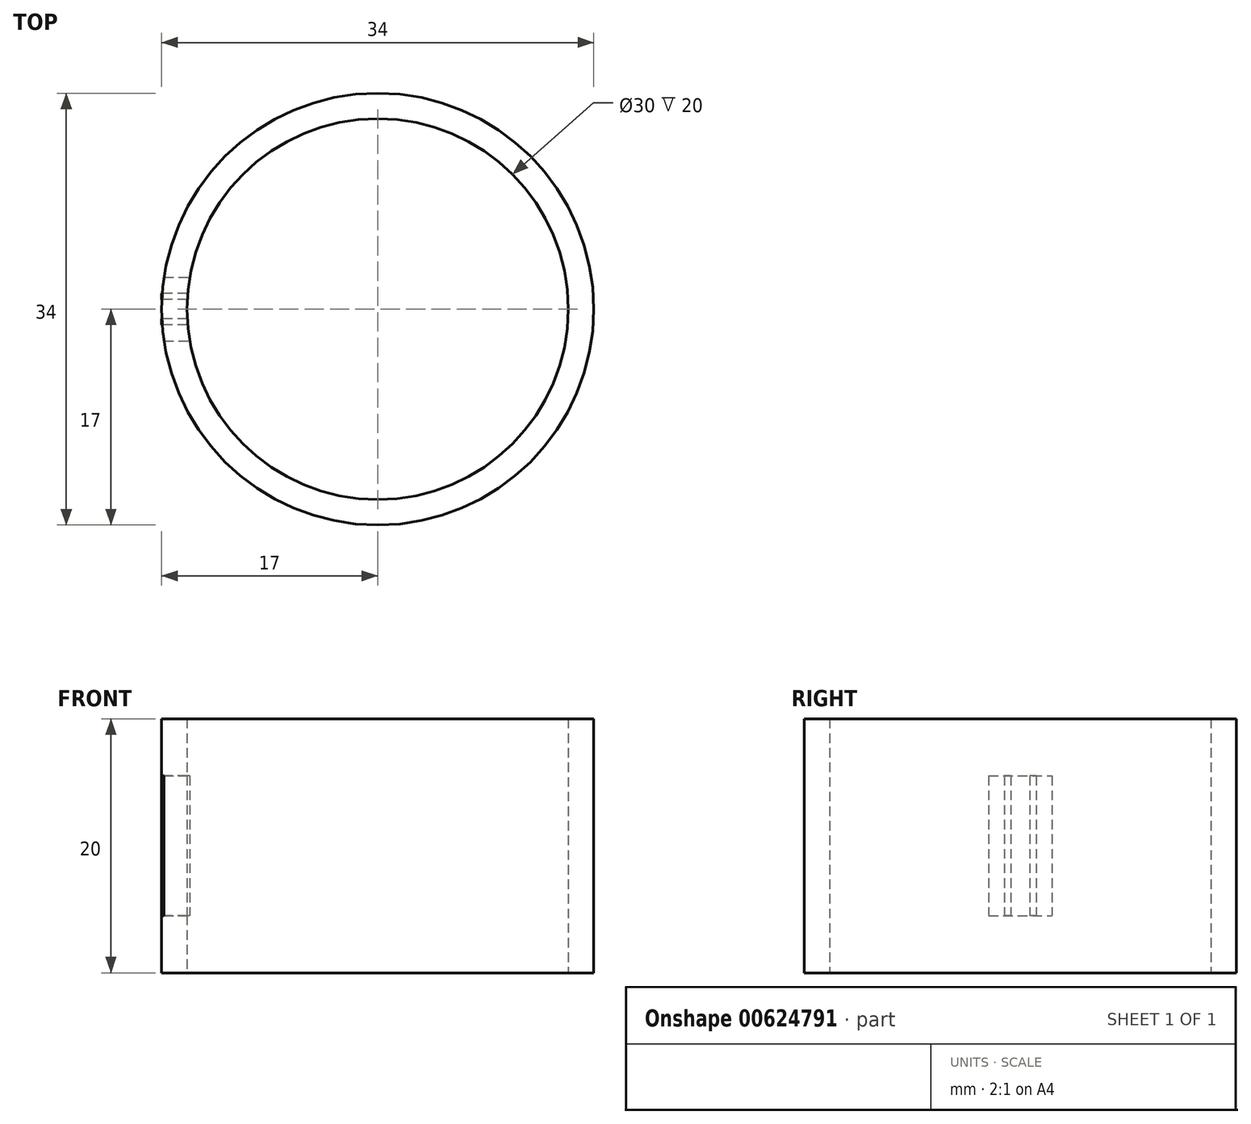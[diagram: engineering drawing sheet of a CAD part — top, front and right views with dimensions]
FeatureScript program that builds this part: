
annotation { "Feature Type Name" : "Feature", "Feature Type Description" : "" }
export const myFeature = defineFeature(function(context is Context, id is Id, definition is map)
    precondition{}
    {
        {
            var Q0;
            Q0=qCreatedBy(makeId("Top.planeOp"),FACE);
            var sketch = newSketch(context, id + "F0", { "sketchPlane" : qUnion([Q0])});
            skCircle(sketch, "E0", {"center": v(0, 0) * mm, "radius": 15 * mm});
            skCircle(sketch, "E1.0", {"center": v(0, 0) * mm, "radius": 17 * mm});
            skSolve(sketch);
        }
        {
            var Q0;
            Q0=makeQuery(id+"F0.imprint","IMPRINT",FACE,{"disambiguationData":[TD([[makeQuery(id+"F0.imprint","IMPRINT",EDGE,{"derivedFrom":sQuery(id+"F0.wireOp",EDGE,"E0")}),-1.0]])]});
            extrude(context, id + "F1", {"entities" : qUnion([Q0]), "depth" : 20 * mm, "offsetDistance" : 25 * mm});
        }
        {
            var Q0;
            Q0=qCreatedBy(makeId("Right.planeOp"),FACE);
            cPlane(context, id + "F2", {"entities" : qUnion([Q0]), "cplaneType" : CPlaneType.OFFSET, "offset" : 17 * mm, "oppositeDirection" : true, "width" : 150 * mm, "height" : 150 * mm});
        }
        {
            var Q0;
            Q0=qCreatedBy(makeId("Right.planeOp"),FACE);
            var sketch = newSketch(context, id + "F3", { "sketchPlane" : qUnion([Q0])});
            skLineSegment(sketch, "E2.bottom", {"start": v(-2.5, 15.5) * mm, "end": v(2.5, 15.5) * mm});
            skLineSegment(sketch, "E2.top", {"start": v(-2.5, 4.5) * mm, "end": v(2.5, 4.5) * mm});
            skLineSegment(sketch, "E2.left", {"start": v(-2.5, 15.5) * mm, "end": v(-2.5, 4.5) * mm});
            skLineSegment(sketch, "E2.right", {"start": v(2.5, 15.5) * mm, "end": v(2.5, 4.5) * mm});
            skLineSegment(sketch, "E3", {"start": v(-17, 10) * mm, "end": v(16.98, 10) * mm, "construction": true});
            skSolve(sketch);
        }
        {
            var Q0;
            Q0 = qSketchRegion(id + "F3", true);
            extrude(context, id + "F4", {"entities" : qUnion([Q0]), "operationType" : NewBodyOperationType.REMOVE, "oppositeDirection" : true, "depth" : 25 * mm, "offsetDistance" : 25 * mm});
        }
        {
            var Q0;
            Q0=qCreatedBy(id+"F2.planeOp",FACE);
            var sketch = newSketch(context, id + "F5", { "sketchPlane" : qUnion([Q0])});
            skLineSegment(sketch, "E4.bottom", {"start": v(-0.75, 15.5) * mm, "end": v(-1.25, 15.5) * mm});
            skLineSegment(sketch, "E4.top", {"start": v(-0.75, 4.5) * mm, "end": v(-1.25, 4.5) * mm});
            skLineSegment(sketch, "E4.left", {"start": v(-0.75, 15.5) * mm, "end": v(-0.75, 4.5) * mm});
            skLineSegment(sketch, "E4.right", {"start": v(-1.25, 15.5) * mm, "end": v(-1.25, 4.5) * mm});
            skLineSegment(sketch, "E5.bottom", {"start": v(1.25, 15.5) * mm, "end": v(0.75, 15.5) * mm});
            skLineSegment(sketch, "E5.top", {"start": v(1.25, 4.5) * mm, "end": v(0.75, 4.5) * mm});
            skLineSegment(sketch, "E5.left", {"start": v(1.25, 15.5) * mm, "end": v(1.25, 4.5) * mm});
            skLineSegment(sketch, "E5.right", {"start": v(0.75, 15.5) * mm, "end": v(0.75, 4.5) * mm});
            skSolve(sketch);
        }
        {
            var Q0;
            Q0 = qSketchRegion(id + "F5", true);
            extrude(context, id + "F6", {"entities" : qUnion([Q0]), "depth" : 2 * mm, "offsetDistance" : 25 * mm});
        }
    });
